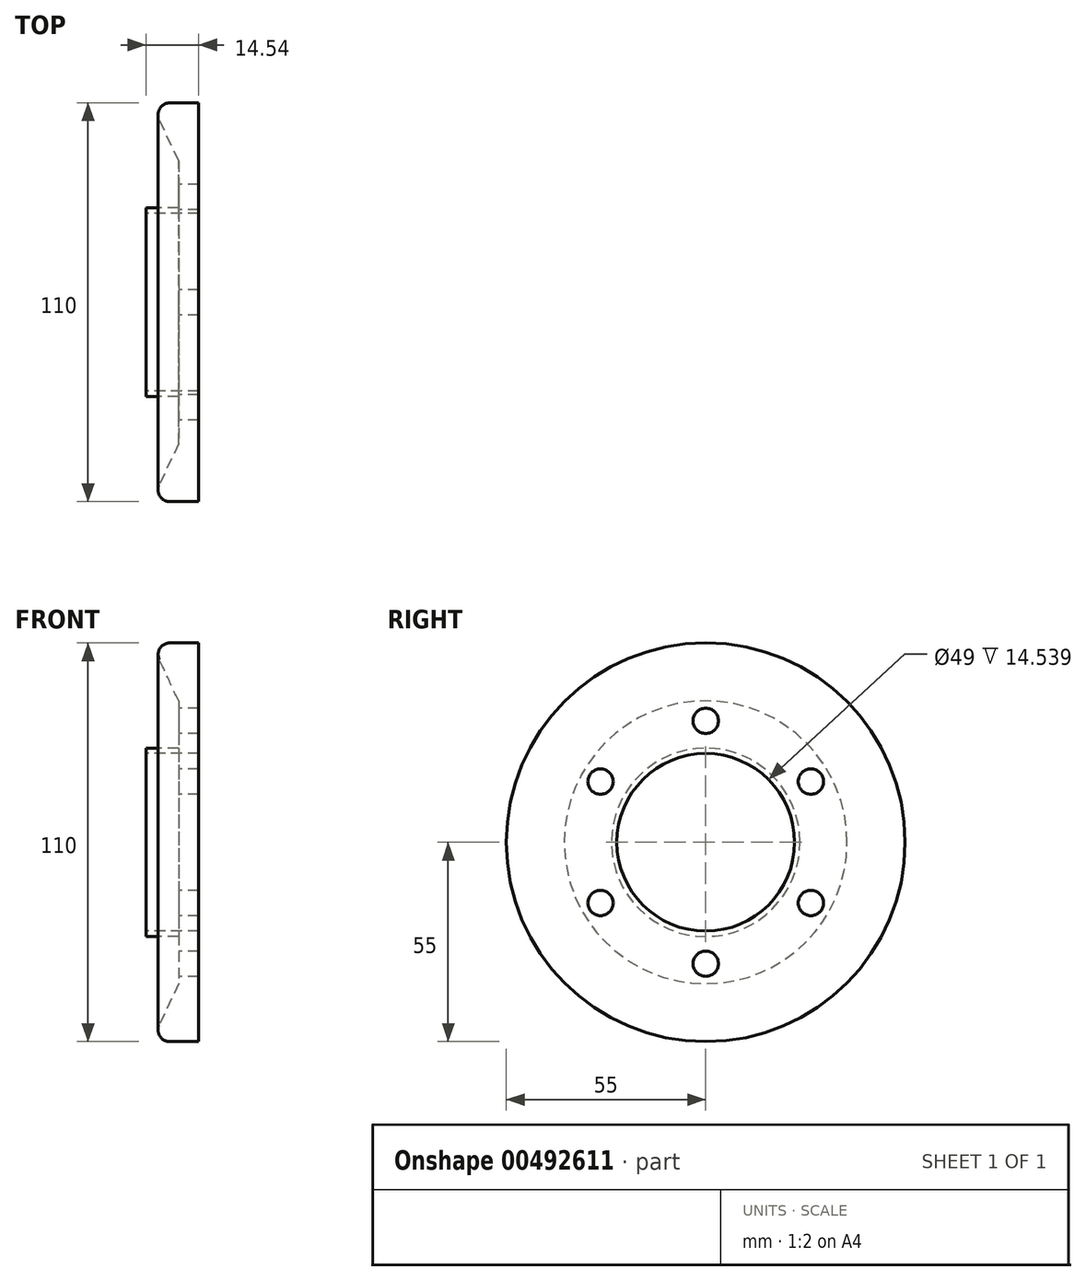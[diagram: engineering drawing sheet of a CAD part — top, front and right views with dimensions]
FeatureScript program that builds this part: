
annotation { "Feature Type Name" : "Feature", "Feature Type Description" : "" }
export const myFeature = defineFeature(function(context is Context, id is Id, definition is map)
    precondition{}
    {
        {
            var Q0;
            Q0=qCreatedBy(makeId("Front.planeOp"),FACE);
            var sketch = newSketch(context, id + "F0", { "sketchPlane" : qUnion([Q0])});
            skLineSegment(sketch, "E0", {"start": v(8.64, 20.25) * mm, "end": v(16.66, 20.25) * mm});
            skLineSegment(sketch, "E1", {"start": v(5.76, 15.73) * mm, "end": v(11.12, 4.25) * mm});
            skLineSegment(sketch, "E2", {"start": v(16.66, 20.25) * mm, "end": v(16.66, 4.25) * mm});
            skArc(sketch, "E3.filletArc", {"start": v(8.64, 20.25) * mm, "mid": v(5.96, 18.78) * mm, "end": v(5.76, 15.73) * mm});
            skLineSegment(sketch, "E4", {"start": v(16.66, 4.25) * mm, "end": v(16.66, -34.75) * mm});
            skLineSegment(sketch, "E5", {"start": v(11.12, 4.25) * mm, "end": v(11.12, -8.75) * mm});
            skLineSegment(sketch, "E6", {"start": v(11.12, -8.75) * mm, "end": v(2.12, -8.75) * mm});
            skLineSegment(sketch, "E7", {"start": v(2.12, -8.75) * mm, "end": v(2.12, -34.75) * mm});
            skLineSegment(sketch, "E8", {"start": v(2.12, -34.75) * mm, "end": v(16.66, -34.75) * mm});
            skSolve(sketch);
        }
        {
            var Q0;
            Q0=makeQuery(id+"F0.imprint","IMPRINT",FACE,{"disambiguationData":[TD([[makeQuery(id+"F0.imprint","IMPRINT",EDGE,{"derivedFrom":sQuery(id+"F0.wireOp",EDGE,"E0")}),-1.0]])]});
            var Q1;
            Q1=sQuery(id+"F0.wireOp",EDGE,"E8");
            revolve(context, id + "F1", {"entities" : qUnion([Q0]), "axis" : qUnion([Q1]), "revolveType" : RevolveType.FULL});
        }
        {
            var Q0;
            Q0=makeQuery(id+"F1.opRevolve","SWEPT_FACE",FACE,{"disambiguationData":[OSD([sQuery(id+"F0.wireOp",EDGE,"E7")])]});
            var sketch = newSketch(context, id + "F2", { "sketchPlane" : qUnion([Q0])});
            skCircle(sketch, "E9", {"center": v(0, -34.75) * mm, "radius": 24.5 * mm});
            skSolve(sketch);
        }
        {
            var Q0;
            Q0=makeQuery(id+"F2.imprint","IMPRINT",FACE,{"disambiguationData":[TD([[makeQuery(id+"F2.imprint","IMPRINT",EDGE,{"derivedFrom":sQuery(id+"F2.wireOp",EDGE,"E9")}),1.0]])]});
            extrude(context, id + "F3", {"entities" : qUnion([Q0]), "operationType" : NewBodyOperationType.REMOVE, "endBound" : BoundingType.THROUGH_ALL, "oppositeDirection" : true, "depth" : 25 * mm});
        }
        {
            var Q0;
            Q0=makeQuery(id+"F1.opRevolve","SWEPT_FACE",FACE,{"disambiguationData":[OSD([sQuery(id+"F0.wireOp",EDGE,"E5")])]});
            var sketch = newSketch(context, id + "F4", { "sketchPlane" : qUnion([Q0])});
            skCircle(sketch, "E10", {"center": v(0, -1.25) * mm, "radius": 3.5 * mm});
            skCircle(sketch, "E11.1.0", {"center": v(-29.01, -18) * mm, "radius": 3.5 * mm});
            skCircle(sketch, "E11.2.0", {"center": v(-29.01, -51.5) * mm, "radius": 3.5 * mm});
            skCircle(sketch, "E11.3.0", {"center": v(0, -68.25) * mm, "radius": 3.5 * mm});
            skCircle(sketch, "E11.4.0", {"center": v(29.01, -51.5) * mm, "radius": 3.5 * mm});
            skCircle(sketch, "E11.5.0", {"center": v(29.01, -18) * mm, "radius": 3.5 * mm});
            skSolve(sketch);
        }
        {
            var Q0;
            Q0=makeQuery(id+"F4.imprint","IMPRINT",FACE,{"disambiguationData":[TD([[makeQuery(id+"F4.imprint","IMPRINT",EDGE,{"derivedFrom":sQuery(id+"F4.wireOp",EDGE,"E10")}),1.0]])]});
            var Q1;
            Q1=makeQuery(id+"F4.imprint","IMPRINT",FACE,{"disambiguationData":[TD([[makeQuery(id+"F4.imprint","IMPRINT",EDGE,{"derivedFrom":sQuery(id+"F4.wireOp",EDGE,"E11.1.0")}),1.0]])]});
            var Q2;
            Q2=makeQuery(id+"F4.imprint","IMPRINT",FACE,{"disambiguationData":[TD([[makeQuery(id+"F4.imprint","IMPRINT",EDGE,{"derivedFrom":sQuery(id+"F4.wireOp",EDGE,"E11.2.0")}),1.0]])]});
            var Q3;
            Q3=makeQuery(id+"F4.imprint","IMPRINT",FACE,{"disambiguationData":[TD([[makeQuery(id+"F4.imprint","IMPRINT",EDGE,{"derivedFrom":sQuery(id+"F4.wireOp",EDGE,"E11.3.0")}),1.0]])]});
            var Q4;
            Q4=makeQuery(id+"F4.imprint","IMPRINT",FACE,{"disambiguationData":[TD([[makeQuery(id+"F4.imprint","IMPRINT",EDGE,{"derivedFrom":sQuery(id+"F4.wireOp",EDGE,"E11.4.0")}),1.0]])]});
            var Q5;
            Q5=makeQuery(id+"F4.imprint","IMPRINT",FACE,{"disambiguationData":[TD([[makeQuery(id+"F4.imprint","IMPRINT",EDGE,{"derivedFrom":sQuery(id+"F4.wireOp",EDGE,"E11.5.0")}),1.0]])]});
            extrude(context, id + "F5", {"entities" : qUnion([Q0, Q1, Q2, Q3, Q4, Q5]), "operationType" : NewBodyOperationType.REMOVE, "endBound" : BoundingType.THROUGH_ALL, "oppositeDirection" : true, "depth" : 25 * mm});
        }
    });
